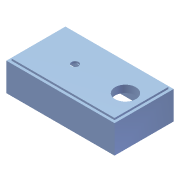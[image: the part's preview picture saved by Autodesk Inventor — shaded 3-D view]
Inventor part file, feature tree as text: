
AUTODESK INVENTOR PART (.ipt)
format: ipt  version: 2012 (Build 160160000, 160)  size: 151,040 bytes
history: native  units: mm
features: extrude x7, sketch x7, projected_geometry x1
ambient origin geometry x8: Origin, YZ Plane, XZ Plane, XY Plane, X Axis, Y Axis, Z Axis, Center Point
bodies: Solid1 (feature_tree)
feature tree (15):
  extrude  "Extrusion1"  Depth=66.2mm
  extrude  "Extrusion2"  Depth=33.1mm
  extrude  "Extrusion3"  Depth=31.5mm TaperAngle=0.0deg
  extrude  "Extrusion4"  Depth=8.1mm
  extrude  "Extrusion5"  Depth=30.2mm
  extrude  "Extrusion6"  Depth=18.0mm
  extrude  "Extrusion7"  Depth=23.282852mm
  sketch  "Sketch1"  dims[d0=121.2mm d1=66.2mm]
  sketch  "Sketch2"  dims[d2=60.6mm d3=33.1mm]
  sketch  "Sketch3"  dims[d4=2.9mm d5=31.5mm d6=0.0mm]
  projected_geometry  "Projected Loop1"
  sketch  "Sketch4"  dims[d7=2.1mm d8=0.0mm d9=8.1mm]
  sketch  "Sketch5"  dims[d10=41.0mm d11=30.2mm]
  sketch  "Sketch6"  dims[d12=30.2mm d13=18.0mm]
  sketch  "Sketch7"  dims[d14=2.1mm d15=0.0mm d16=23.282852mm d17=26.282852mm d18=6.0mm d19=0.0mm d20=9.1mm d21=31.8mm d22=0.0mm d23=2.4mm d24=0.0mm d25=5.1mm d26=29.0mm d27=0.0mm d28=60.4mm d29=24.6mm d30=65.6mm d31=8.1mm d32=41.0mm d33=13.25mm d34=20.0mm d36=23.95mm d37=8.1mm d39=9.0mm d40=0.0mm d41=115.4mm d42=60.4mm d43=56.4mm]
